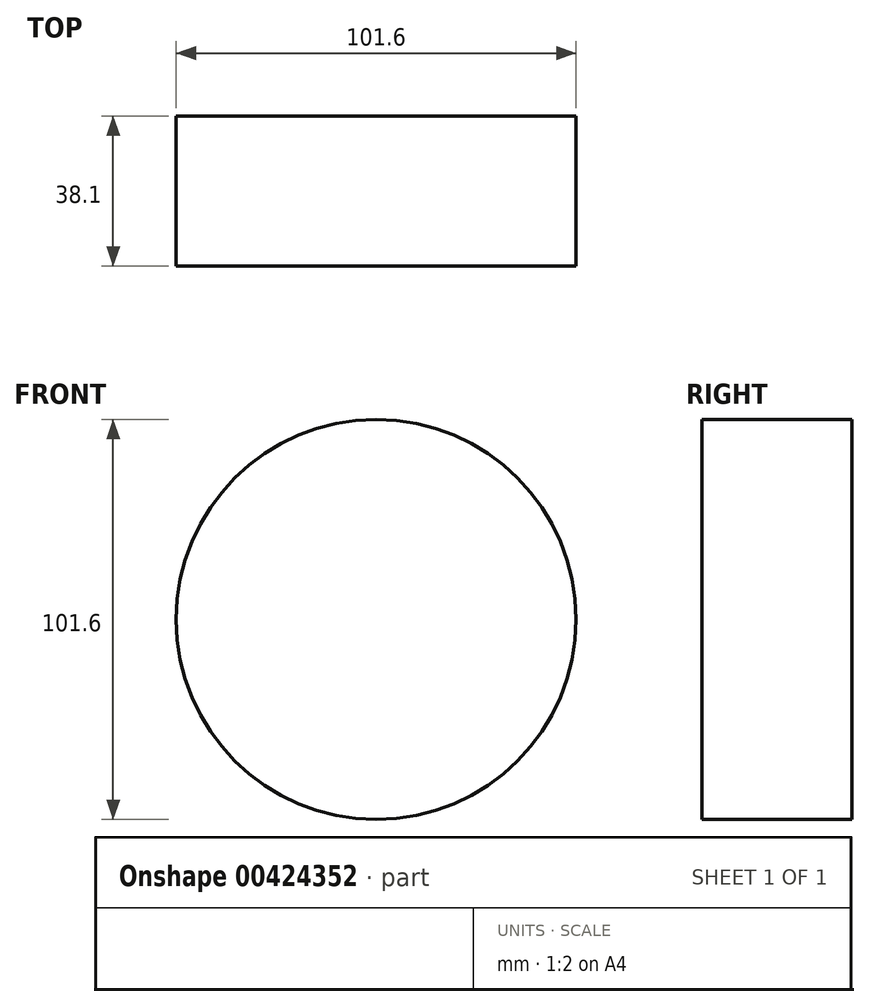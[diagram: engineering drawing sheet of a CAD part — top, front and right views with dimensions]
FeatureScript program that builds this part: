
annotation { "Feature Type Name" : "Feature", "Feature Type Description" : "" }
export const myFeature = defineFeature(function(context is Context, id is Id, definition is map)
    precondition{}
    {
        {
            var Q0;
            Q0=qCreatedBy(makeId("Front.planeOp"),FACE);
            var sketch = newSketch(context, id + "F0", { "sketchPlane" : qUnion([Q0])});
            skCircle(sketch, "E0", {"center": v(0, 0) * mm, "radius": 50.8 * mm});
            skSolve(sketch);
        }
        {
            var Q0;
            Q0=makeQuery(id+"F0.imprint","IMPRINT",FACE,{"disambiguationData":[TD([[makeQuery(id+"F0.imprint","IMPRINT",EDGE,{"derivedFrom":sQuery(id+"F0.wireOp",EDGE,"E0")}),1.0]])]});
            extrude(context, id + "F1", {"entities" : qUnion([Q0]), "depth" : 38.1 * mm});
        }
    });
